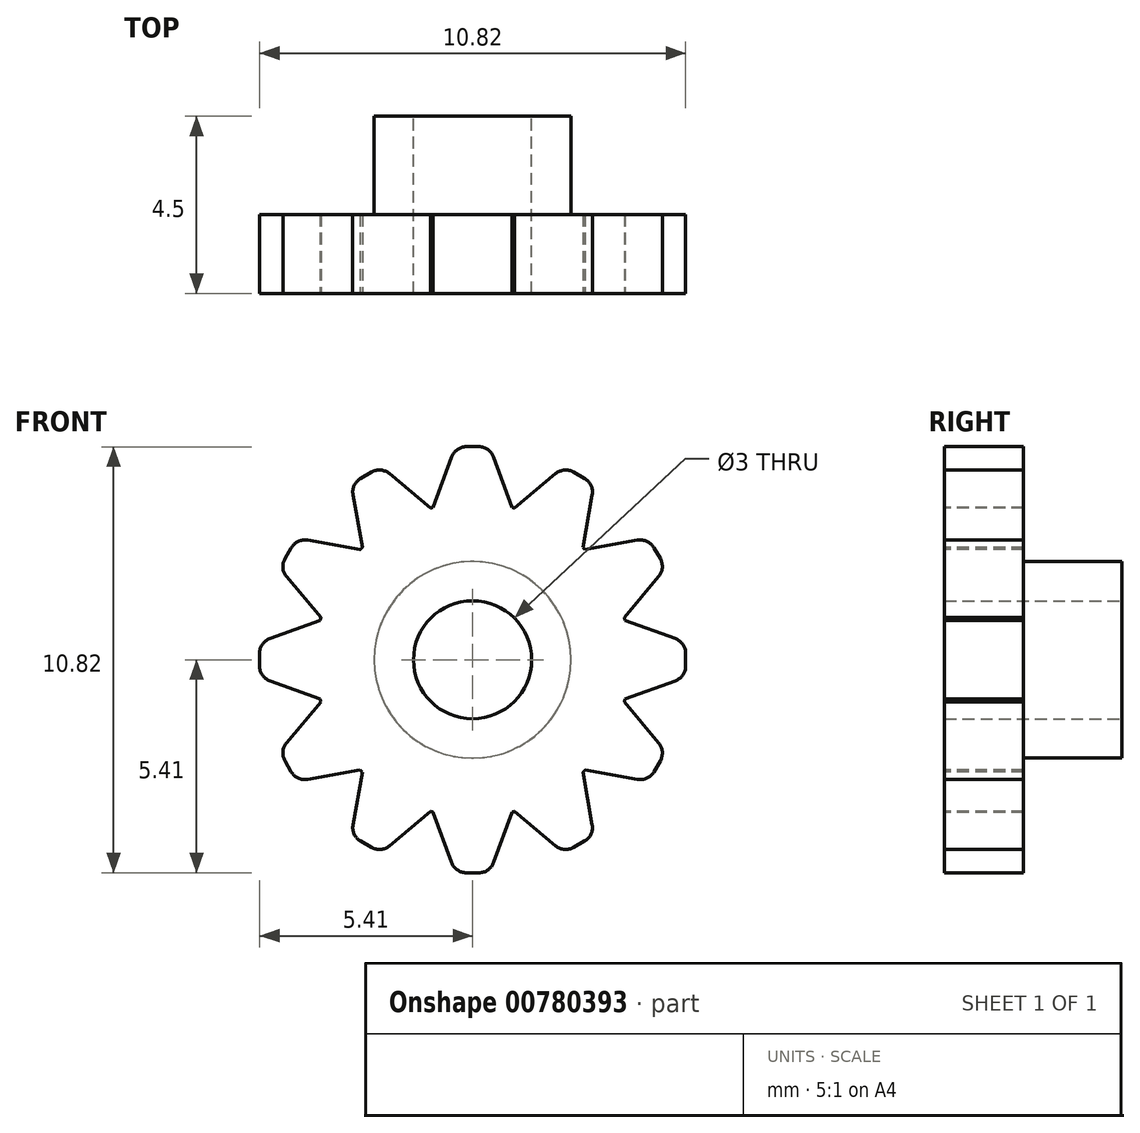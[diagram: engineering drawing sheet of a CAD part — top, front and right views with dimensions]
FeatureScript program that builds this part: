
annotation { "Feature Type Name" : "Feature", "Feature Type Description" : "" }
export const myFeature = defineFeature(function(context is Context, id is Id, definition is map)
    precondition{}
    {
        {
            var Q0;
            Q0=qCreatedBy(makeId("Front.planeOp"),FACE);
            var sketch = newSketch(context, id + "F0", { "sketchPlane" : qUnion([Q0])});
            skCircle(sketch, "E0", {"center": v(0, 0) * mm, "radius": 4 * mm});
            skCircle(sketch, "E1", {"center": v(0, 0) * mm, "radius": 1.5 * mm});
            skSolve(sketch);
        }
        {
            var Q0;
            Q0=qSketchRegion(id+"F0",true);
            extrude(context, id + "F1", {"entities" : qUnion([Q0]), "depth" : 2 * mm, "offsetDistance" : 25 * mm});
        }
        {
            var Q0;
            Q0=makeQuery(id+"F1.opExtrude","CAP_FACE",FACE,{"disambiguationData":[OSD([sQuery(id+"F0.wireOp",EDGE,"E0")])],"isStart":false});
            var sketch = newSketch(context, id + "F2", { "sketchPlane" : qUnion([Q0])});
            skLineSegment(sketch, "E2", {"start": v(0, 0) * mm, "end": v(0, 7.76) * mm, "construction": true});
            skLineSegment(sketch, "E3", {"start": v(0, 5.41) * mm, "end": v(0.44, 5.41) * mm});
            skLineSegment(sketch, "E4", {"start": v(0.44, 5.41) * mm, "end": v(1, 3.87) * mm});
            skLineSegment(sketch, "E5.MirrorCS", {"start": v(0, 5.41) * mm, "end": v(-0.44, 5.41) * mm});
            skLineSegment(sketch, "E6.MirrorCS", {"start": v(-0.44, 5.41) * mm, "end": v(-1, 3.87) * mm});
            skLineSegment(sketch, "E7", {"start": v(-1, 3.87) * mm, "end": v(1, 3.87) * mm});
            skLineSegment(sketch, "E8.1.0", {"start": v(-2.8, 2.85) * mm, "end": v(-1.07, 3.85) * mm});
            skLineSegment(sketch, "E8.1.1", {"start": v(-3.09, 4.47) * mm, "end": v(-2.8, 2.85) * mm});
            skLineSegment(sketch, "E8.1.2", {"start": v(-2.33, 4.9) * mm, "end": v(-1.07, 3.85) * mm});
            skLineSegment(sketch, "E8.1.3", {"start": v(-2.7, 4.69) * mm, "end": v(-2.33, 4.9) * mm});
            skLineSegment(sketch, "E8.1.4", {"start": v(-2.7, 4.69) * mm, "end": v(-3.09, 4.47) * mm});
            skLineSegment(sketch, "E8.2.0", {"start": v(-3.85, 1.07) * mm, "end": v(-2.85, 2.8) * mm});
            skLineSegment(sketch, "E8.2.1", {"start": v(-4.9, 2.33) * mm, "end": v(-3.85, 1.07) * mm});
            skLineSegment(sketch, "E8.2.2", {"start": v(-4.47, 3.09) * mm, "end": v(-2.85, 2.8) * mm});
            skLineSegment(sketch, "E8.2.3", {"start": v(-4.69, 2.7) * mm, "end": v(-4.47, 3.09) * mm});
            skLineSegment(sketch, "E8.2.4", {"start": v(-4.69, 2.7) * mm, "end": v(-4.9, 2.33) * mm});
            skLineSegment(sketch, "E8.3.0", {"start": v(-3.87, -1) * mm, "end": v(-3.87, 1) * mm});
            skLineSegment(sketch, "E8.3.1", {"start": v(-5.41, -0.44) * mm, "end": v(-3.87, -1) * mm});
            skLineSegment(sketch, "E8.3.2", {"start": v(-5.41, 0.44) * mm, "end": v(-3.87, 1) * mm});
            skLineSegment(sketch, "E8.3.3", {"start": v(-5.41, 0) * mm, "end": v(-5.41, 0.44) * mm});
            skLineSegment(sketch, "E8.3.4", {"start": v(-5.41, 0) * mm, "end": v(-5.41, -0.44) * mm});
            skLineSegment(sketch, "E8.4.0", {"start": v(-2.85, -2.8) * mm, "end": v(-3.85, -1.07) * mm});
            skLineSegment(sketch, "E8.4.1", {"start": v(-4.47, -3.09) * mm, "end": v(-2.85, -2.8) * mm});
            skLineSegment(sketch, "E8.4.2", {"start": v(-4.9, -2.33) * mm, "end": v(-3.85, -1.07) * mm});
            skLineSegment(sketch, "E8.4.3", {"start": v(-4.69, -2.7) * mm, "end": v(-4.9, -2.33) * mm});
            skLineSegment(sketch, "E8.4.4", {"start": v(-4.69, -2.7) * mm, "end": v(-4.47, -3.09) * mm});
            skLineSegment(sketch, "E8.5.0", {"start": v(-1.07, -3.85) * mm, "end": v(-2.8, -2.85) * mm});
            skLineSegment(sketch, "E8.5.1", {"start": v(-2.33, -4.9) * mm, "end": v(-1.07, -3.85) * mm});
            skLineSegment(sketch, "E8.5.2", {"start": v(-3.09, -4.47) * mm, "end": v(-2.8, -2.85) * mm});
            skLineSegment(sketch, "E8.5.3", {"start": v(-2.7, -4.69) * mm, "end": v(-3.09, -4.47) * mm});
            skLineSegment(sketch, "E8.5.4", {"start": v(-2.7, -4.69) * mm, "end": v(-2.33, -4.9) * mm});
            skLineSegment(sketch, "E8.6.0", {"start": v(1, -3.87) * mm, "end": v(-1, -3.87) * mm});
            skLineSegment(sketch, "E8.6.1", {"start": v(0.44, -5.41) * mm, "end": v(1, -3.87) * mm});
            skLineSegment(sketch, "E8.6.2", {"start": v(-0.44, -5.41) * mm, "end": v(-1, -3.87) * mm});
            skLineSegment(sketch, "E8.6.3", {"start": v(0, -5.41) * mm, "end": v(-0.44, -5.41) * mm});
            skLineSegment(sketch, "E8.6.4", {"start": v(0, -5.41) * mm, "end": v(0.44, -5.41) * mm});
            skLineSegment(sketch, "E8.7.0", {"start": v(2.8, -2.85) * mm, "end": v(1.07, -3.85) * mm});
            skLineSegment(sketch, "E8.7.1", {"start": v(3.09, -4.47) * mm, "end": v(2.8, -2.85) * mm});
            skLineSegment(sketch, "E8.7.2", {"start": v(2.33, -4.9) * mm, "end": v(1.07, -3.85) * mm});
            skLineSegment(sketch, "E8.7.3", {"start": v(2.7, -4.69) * mm, "end": v(2.33, -4.9) * mm});
            skLineSegment(sketch, "E8.7.4", {"start": v(2.7, -4.69) * mm, "end": v(3.09, -4.47) * mm});
            skLineSegment(sketch, "E8.8.0", {"start": v(3.85, -1.07) * mm, "end": v(2.85, -2.8) * mm});
            skLineSegment(sketch, "E8.8.1", {"start": v(4.9, -2.33) * mm, "end": v(3.85, -1.07) * mm});
            skLineSegment(sketch, "E8.8.2", {"start": v(4.47, -3.09) * mm, "end": v(2.85, -2.8) * mm});
            skLineSegment(sketch, "E8.8.3", {"start": v(4.69, -2.7) * mm, "end": v(4.47, -3.09) * mm});
            skLineSegment(sketch, "E8.8.4", {"start": v(4.69, -2.7) * mm, "end": v(4.9, -2.33) * mm});
            skLineSegment(sketch, "E8.9.0", {"start": v(3.87, 1) * mm, "end": v(3.87, -1) * mm});
            skLineSegment(sketch, "E8.9.1", {"start": v(5.41, 0.44) * mm, "end": v(3.87, 1) * mm});
            skLineSegment(sketch, "E8.9.2", {"start": v(5.41, -0.44) * mm, "end": v(3.87, -1) * mm});
            skLineSegment(sketch, "E8.9.3", {"start": v(5.41, 0) * mm, "end": v(5.41, -0.44) * mm});
            skLineSegment(sketch, "E8.9.4", {"start": v(5.41, 0) * mm, "end": v(5.41, 0.44) * mm});
            skLineSegment(sketch, "E8.10.0", {"start": v(2.85, 2.8) * mm, "end": v(3.85, 1.07) * mm});
            skLineSegment(sketch, "E8.10.1", {"start": v(4.47, 3.09) * mm, "end": v(2.85, 2.8) * mm});
            skLineSegment(sketch, "E8.10.2", {"start": v(4.9, 2.33) * mm, "end": v(3.85, 1.07) * mm});
            skLineSegment(sketch, "E8.10.3", {"start": v(4.69, 2.7) * mm, "end": v(4.9, 2.33) * mm});
            skLineSegment(sketch, "E8.10.4", {"start": v(4.69, 2.7) * mm, "end": v(4.47, 3.09) * mm});
            skLineSegment(sketch, "E8.11.0", {"start": v(1.07, 3.85) * mm, "end": v(2.8, 2.85) * mm});
            skLineSegment(sketch, "E8.11.1", {"start": v(2.33, 4.9) * mm, "end": v(1.07, 3.85) * mm});
            skLineSegment(sketch, "E8.11.2", {"start": v(3.09, 4.47) * mm, "end": v(2.8, 2.85) * mm});
            skLineSegment(sketch, "E8.11.3", {"start": v(2.7, 4.69) * mm, "end": v(3.09, 4.47) * mm});
            skLineSegment(sketch, "E8.11.4", {"start": v(2.7, 4.69) * mm, "end": v(2.33, 4.9) * mm});
            skPoint(sketch, "E8.center", {"position": v(0, 0) * mm});
            skSolve(sketch);
        }
        {
            var Q0;
            Q0=qSketchRegion(id+"F2",true);
            var Q1;
            Q1=makeQuery(id+"F1.opExtrude","CAP_FACE",FACE,{"disambiguationData":[OSD([sQuery(id+"F0.wireOp",EDGE,"E0"),sQuery(id+"F0.wireOp",EDGE,"E1")])],"isStart":true});
            extrude(context, id + "F3", {"entities" : qUnion([Q0]), "operationType" : NewBodyOperationType.ADD, "endBound" : BoundingType.UP_TO_SURFACE, "oppositeDirection" : true, "depth" : 2 * mm, "endBoundEntityFace" : qUnion([Q1]), "offsetDistance" : 25 * mm});
        }
        {
            var Q0;
            Q0=makeQuery(id+"F3.boolean.opBoolean","MERGE",FACE,{"derivedFrom":[makeQuery(id+"F1.opExtrude","CAP_FACE",FACE,{"disambiguationData":[OSD([sQuery(id+"F0.wireOp",EDGE,"E0"),sQuery(id+"F0.wireOp",EDGE,"E1")])],"isStart":true}),makeQuery(id+"F3.opExtrude","CAP_FACE",FACE,{"disambiguationData":[OSD([sQuery(id+"F2.wireOp",EDGE,"E3"),sQuery(id+"F2.wireOp",EDGE,"E4"),sQuery(id+"F2.wireOp",EDGE,"E5.MirrorCS"),sQuery(id+"F2.wireOp",EDGE,"E6.MirrorCS"),sQuery(id+"F2.wireOp",EDGE,"E7")])],"isStart":false}),makeQuery(id+"F3.opExtrude","CAP_FACE",FACE,{"disambiguationData":[OSD([sQuery(id+"F2.wireOp",EDGE,"E8.1.0"),sQuery(id+"F2.wireOp",EDGE,"E8.1.1"),sQuery(id+"F2.wireOp",EDGE,"E8.1.2"),sQuery(id+"F2.wireOp",EDGE,"E8.1.3"),sQuery(id+"F2.wireOp",EDGE,"E8.1.4")])],"isStart":false}),makeQuery(id+"F3.opExtrude","CAP_FACE",FACE,{"disambiguationData":[OSD([sQuery(id+"F2.wireOp",EDGE,"E8.2.0"),sQuery(id+"F2.wireOp",EDGE,"E8.2.1"),sQuery(id+"F2.wireOp",EDGE,"E8.2.2"),sQuery(id+"F2.wireOp",EDGE,"E8.2.3"),sQuery(id+"F2.wireOp",EDGE,"E8.2.4")])],"isStart":false}),makeQuery(id+"F3.opExtrude","CAP_FACE",FACE,{"disambiguationData":[OSD([sQuery(id+"F2.wireOp",EDGE,"E8.3.0"),sQuery(id+"F2.wireOp",EDGE,"E8.3.1"),sQuery(id+"F2.wireOp",EDGE,"E8.3.2"),sQuery(id+"F2.wireOp",EDGE,"E8.3.3"),sQuery(id+"F2.wireOp",EDGE,"E8.3.4")])],"isStart":false}),makeQuery(id+"F3.opExtrude","CAP_FACE",FACE,{"disambiguationData":[OSD([sQuery(id+"F2.wireOp",EDGE,"E8.4.0"),sQuery(id+"F2.wireOp",EDGE,"E8.4.1"),sQuery(id+"F2.wireOp",EDGE,"E8.4.2"),sQuery(id+"F2.wireOp",EDGE,"E8.4.3"),sQuery(id+"F2.wireOp",EDGE,"E8.4.4")])],"isStart":false}),makeQuery(id+"F3.opExtrude","CAP_FACE",FACE,{"disambiguationData":[OSD([sQuery(id+"F2.wireOp",EDGE,"E8.5.0"),sQuery(id+"F2.wireOp",EDGE,"E8.5.1"),sQuery(id+"F2.wireOp",EDGE,"E8.5.2"),sQuery(id+"F2.wireOp",EDGE,"E8.5.3"),sQuery(id+"F2.wireOp",EDGE,"E8.5.4")])],"isStart":false}),makeQuery(id+"F3.opExtrude","CAP_FACE",FACE,{"disambiguationData":[OSD([sQuery(id+"F2.wireOp",EDGE,"E8.6.0"),sQuery(id+"F2.wireOp",EDGE,"E8.6.1"),sQuery(id+"F2.wireOp",EDGE,"E8.6.2"),sQuery(id+"F2.wireOp",EDGE,"E8.6.3"),sQuery(id+"F2.wireOp",EDGE,"E8.6.4")])],"isStart":false}),makeQuery(id+"F3.opExtrude","CAP_FACE",FACE,{"disambiguationData":[OSD([sQuery(id+"F2.wireOp",EDGE,"E8.7.0"),sQuery(id+"F2.wireOp",EDGE,"E8.7.1"),sQuery(id+"F2.wireOp",EDGE,"E8.7.2"),sQuery(id+"F2.wireOp",EDGE,"E8.7.3"),sQuery(id+"F2.wireOp",EDGE,"E8.7.4")])],"isStart":false}),makeQuery(id+"F3.opExtrude","CAP_FACE",FACE,{"disambiguationData":[OSD([sQuery(id+"F2.wireOp",EDGE,"E8.8.0"),sQuery(id+"F2.wireOp",EDGE,"E8.8.1"),sQuery(id+"F2.wireOp",EDGE,"E8.8.2"),sQuery(id+"F2.wireOp",EDGE,"E8.8.3"),sQuery(id+"F2.wireOp",EDGE,"E8.8.4")])],"isStart":false}),makeQuery(id+"F3.opExtrude","CAP_FACE",FACE,{"disambiguationData":[OSD([sQuery(id+"F2.wireOp",EDGE,"E8.9.0"),sQuery(id+"F2.wireOp",EDGE,"E8.9.1"),sQuery(id+"F2.wireOp",EDGE,"E8.9.2"),sQuery(id+"F2.wireOp",EDGE,"E8.9.3"),sQuery(id+"F2.wireOp",EDGE,"E8.9.4")])],"isStart":false}),makeQuery(id+"F3.opExtrude","CAP_FACE",FACE,{"disambiguationData":[OSD([sQuery(id+"F2.wireOp",EDGE,"E8.10.0"),sQuery(id+"F2.wireOp",EDGE,"E8.10.1"),sQuery(id+"F2.wireOp",EDGE,"E8.10.2"),sQuery(id+"F2.wireOp",EDGE,"E8.10.3"),sQuery(id+"F2.wireOp",EDGE,"E8.10.4")])],"isStart":false}),makeQuery(id+"F3.opExtrude","CAP_FACE",FACE,{"disambiguationData":[OSD([sQuery(id+"F2.wireOp",EDGE,"E8.11.0"),sQuery(id+"F2.wireOp",EDGE,"E8.11.1"),sQuery(id+"F2.wireOp",EDGE,"E8.11.2"),sQuery(id+"F2.wireOp",EDGE,"E8.11.3"),sQuery(id+"F2.wireOp",EDGE,"E8.11.4")])],"isStart":false})]});
            var sketch = newSketch(context, id + "F4", { "sketchPlane" : qUnion([Q0])});
            skCircle(sketch, "E9.0", {"center": v(0, 0) * mm, "radius": 1.5 * mm});
            skCircle(sketch, "E10.0", {"center": v(0, 0) * mm, "radius": 2.5 * mm});
            skSolve(sketch);
        }
        {
            var Q0;
            Q0=qSketchRegion(id+"F4",true);
            extrude(context, id + "F5", {"entities" : qUnion([Q0]), "operationType" : NewBodyOperationType.ADD, "depth" : 2.5 * mm, "offsetDistance" : 25 * mm});
        }
        {
            var Q0;
            Q0=makeQuery(id+"F3.opExtrude","SWEPT_EDGE",EDGE,{"disambiguationData":[OSD([sQuery(id+"F2.wireOp",EDGE,"E8.11.1"),sQuery(id+"F2.wireOp",EDGE,"E8.11.4")])]});
            var Q1;
            Q1=makeQuery(id+"F3.opExtrude","SWEPT_EDGE",EDGE,{"disambiguationData":[OSD([sQuery(id+"F2.wireOp",EDGE,"E8.11.2"),sQuery(id+"F2.wireOp",EDGE,"E8.11.3")])]});
            var Q2;
            Q2=makeQuery(id+"F3.opExtrude","SWEPT_EDGE",EDGE,{"disambiguationData":[OSD([sQuery(id+"F2.wireOp",EDGE,"E8.10.1"),sQuery(id+"F2.wireOp",EDGE,"E8.10.4")])]});
            var Q3;
            Q3=makeQuery(id+"F3.opExtrude","SWEPT_EDGE",EDGE,{"disambiguationData":[OSD([sQuery(id+"F2.wireOp",EDGE,"E8.10.2"),sQuery(id+"F2.wireOp",EDGE,"E8.10.3")])]});
            var Q4;
            Q4=makeQuery(id+"F3.opExtrude","SWEPT_EDGE",EDGE,{"disambiguationData":[OSD([sQuery(id+"F2.wireOp",EDGE,"E8.9.1"),sQuery(id+"F2.wireOp",EDGE,"E8.9.4")])]});
            var Q5;
            Q5=makeQuery(id+"F3.opExtrude","SWEPT_EDGE",EDGE,{"disambiguationData":[OSD([sQuery(id+"F2.wireOp",EDGE,"E8.9.2"),sQuery(id+"F2.wireOp",EDGE,"E8.9.3")])]});
            var Q6;
            Q6=makeQuery(id+"F3.opExtrude","SWEPT_EDGE",EDGE,{"disambiguationData":[OSD([sQuery(id+"F2.wireOp",EDGE,"E8.8.1"),sQuery(id+"F2.wireOp",EDGE,"E8.8.4")])]});
            var Q7;
            Q7=makeQuery(id+"F3.opExtrude","SWEPT_EDGE",EDGE,{"disambiguationData":[OSD([sQuery(id+"F2.wireOp",EDGE,"E8.8.2"),sQuery(id+"F2.wireOp",EDGE,"E8.8.3")])]});
            var Q8;
            Q8=makeQuery(id+"F3.opExtrude","SWEPT_EDGE",EDGE,{"disambiguationData":[OSD([sQuery(id+"F2.wireOp",EDGE,"E8.7.1"),sQuery(id+"F2.wireOp",EDGE,"E8.7.4")])]});
            var Q9;
            Q9=makeQuery(id+"F3.opExtrude","SWEPT_EDGE",EDGE,{"disambiguationData":[OSD([sQuery(id+"F2.wireOp",EDGE,"E8.7.2"),sQuery(id+"F2.wireOp",EDGE,"E8.7.3")])]});
            var Q10;
            Q10=makeQuery(id+"F3.opExtrude","SWEPT_EDGE",EDGE,{"disambiguationData":[OSD([sQuery(id+"F2.wireOp",EDGE,"E8.6.1"),sQuery(id+"F2.wireOp",EDGE,"E8.6.4")])]});
            var Q11;
            Q11=makeQuery(id+"F3.opExtrude","SWEPT_EDGE",EDGE,{"disambiguationData":[OSD([sQuery(id+"F2.wireOp",EDGE,"E8.6.2"),sQuery(id+"F2.wireOp",EDGE,"E8.6.3")])]});
            var Q12;
            Q12=makeQuery(id+"F3.opExtrude","SWEPT_EDGE",EDGE,{"disambiguationData":[OSD([sQuery(id+"F2.wireOp",EDGE,"E8.5.1"),sQuery(id+"F2.wireOp",EDGE,"E8.5.4")])]});
            var Q13;
            Q13=makeQuery(id+"F3.opExtrude","SWEPT_EDGE",EDGE,{"disambiguationData":[OSD([sQuery(id+"F2.wireOp",EDGE,"E8.5.2"),sQuery(id+"F2.wireOp",EDGE,"E8.5.3")])]});
            var Q14;
            Q14=makeQuery(id+"F3.opExtrude","SWEPT_EDGE",EDGE,{"disambiguationData":[OSD([sQuery(id+"F2.wireOp",EDGE,"E8.4.1"),sQuery(id+"F2.wireOp",EDGE,"E8.4.4")])]});
            var Q15;
            Q15=makeQuery(id+"F3.opExtrude","SWEPT_EDGE",EDGE,{"disambiguationData":[OSD([sQuery(id+"F2.wireOp",EDGE,"E8.4.2"),sQuery(id+"F2.wireOp",EDGE,"E8.4.3")])]});
            var Q16;
            Q16=makeQuery(id+"F3.opExtrude","SWEPT_EDGE",EDGE,{"disambiguationData":[OSD([sQuery(id+"F2.wireOp",EDGE,"E8.3.1"),sQuery(id+"F2.wireOp",EDGE,"E8.3.4")])]});
            var Q17;
            Q17=makeQuery(id+"F3.opExtrude","SWEPT_EDGE",EDGE,{"disambiguationData":[OSD([sQuery(id+"F2.wireOp",EDGE,"E8.3.2"),sQuery(id+"F2.wireOp",EDGE,"E8.3.3")])]});
            var Q18;
            Q18=makeQuery(id+"F3.opExtrude","SWEPT_EDGE",EDGE,{"disambiguationData":[OSD([sQuery(id+"F2.wireOp",EDGE,"E8.2.1"),sQuery(id+"F2.wireOp",EDGE,"E8.2.4")])]});
            var Q19;
            Q19=makeQuery(id+"F3.opExtrude","SWEPT_EDGE",EDGE,{"disambiguationData":[OSD([sQuery(id+"F2.wireOp",EDGE,"E8.2.2"),sQuery(id+"F2.wireOp",EDGE,"E8.2.3")])]});
            var Q20;
            Q20=makeQuery(id+"F3.opExtrude","SWEPT_EDGE",EDGE,{"disambiguationData":[OSD([sQuery(id+"F2.wireOp",EDGE,"E8.1.1"),sQuery(id+"F2.wireOp",EDGE,"E8.1.4")])]});
            var Q21;
            Q21=makeQuery(id+"F3.opExtrude","SWEPT_EDGE",EDGE,{"disambiguationData":[OSD([sQuery(id+"F2.wireOp",EDGE,"E8.1.2"),sQuery(id+"F2.wireOp",EDGE,"E8.1.3")])]});
            var Q22;
            Q22=makeQuery(id+"F3.opExtrude","SWEPT_EDGE",EDGE,{"disambiguationData":[OSD([sQuery(id+"F2.wireOp",EDGE,"E5.MirrorCS"),sQuery(id+"F2.wireOp",EDGE,"E6.MirrorCS")])]});
            var Q23;
            Q23=makeQuery(id+"F3.opExtrude","SWEPT_EDGE",EDGE,{"disambiguationData":[OSD([sQuery(id+"F2.wireOp",EDGE,"E3"),sQuery(id+"F2.wireOp",EDGE,"E4")])]});
            fillet(context, id + "F6", {"entities" : qUnion([Q0, Q1, Q2, Q3, Q4, Q5, Q6, Q7, Q8, Q9, Q10, Q11, Q12, Q13, Q14, Q15, Q16, Q17, Q18, Q19, Q20, Q21, Q22, Q23]), "radius" : 0.4 * mm, "tangentPropagation" : true, "allowEdgeOverflow" : false});
        }
    });
